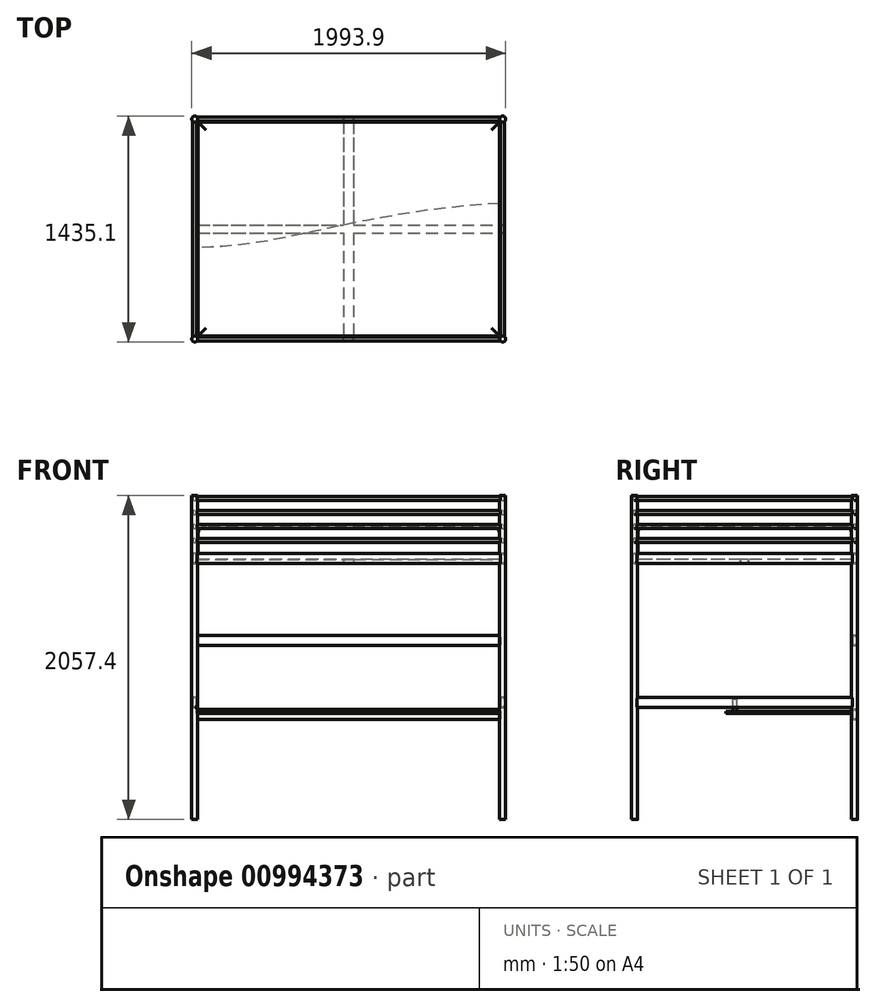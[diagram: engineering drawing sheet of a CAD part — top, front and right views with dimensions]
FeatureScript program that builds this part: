
annotation { "Feature Type Name" : "Feature", "Feature Type Description" : "" }
export const myFeature = defineFeature(function(context is Context, id is Id, definition is map)
    precondition{}
    {
        {
            var Q0;
            Q0=qCreatedBy(makeId("Top.planeOp"),FACE);
            var sketch = newSketch(context, id + "F0", { "sketchPlane" : qUnion([Q0])});
            skLineSegment(sketch, "E0.bottom", {"start": v(977.9, 698.5) * mm, "end": v(-977.9, 698.5) * mm, "construction": true});
            skLineSegment(sketch, "E0.top", {"start": v(977.9, -698.5) * mm, "end": v(-977.9, -698.5) * mm, "construction": true});
            skLineSegment(sketch, "E0.left", {"start": v(977.9, 698.5) * mm, "end": v(977.9, -698.5) * mm, "construction": true});
            skLineSegment(sketch, "E0.right", {"start": v(-977.9, 698.5) * mm, "end": v(-977.9, -698.5) * mm, "construction": true});
            skPoint(sketch, "E0.middle", {"position": v(0, 0) * mm});
            skCircle(sketch, "E1", {"center": v(-977.9, 698.5) * mm, "radius": 19.05 * mm});
            skCircle(sketch, "E2", {"center": v(977.9, 698.5) * mm, "radius": 19.05 * mm});
            skCircle(sketch, "E3", {"center": v(977.9, -698.5) * mm, "radius": 19.05 * mm});
            skCircle(sketch, "E4", {"center": v(-977.9, -698.5) * mm, "radius": 19.05 * mm});
            skSolve(sketch);
        }
        {
            var Q0;
            Q0=makeQuery(id+"F0.imprint","IMPRINT",FACE,{"disambiguationData":[TD([[makeQuery(id+"F0.imprint","IMPRINT",EDGE,{"derivedFrom":sQuery(id+"F0.wireOp",EDGE,"E1")}),1.0]])]});
            var Q1;
            Q1=makeQuery(id+"F0.imprint","IMPRINT",FACE,{"disambiguationData":[TD([[makeQuery(id+"F0.imprint","IMPRINT",EDGE,{"derivedFrom":sQuery(id+"F0.wireOp",EDGE,"E2")}),1.0]])]});
            var Q2;
            Q2=makeQuery(id+"F0.imprint","IMPRINT",FACE,{"disambiguationData":[TD([[makeQuery(id+"F0.imprint","IMPRINT",EDGE,{"derivedFrom":sQuery(id+"F0.wireOp",EDGE,"E3")}),1.0]])]});
            var Q3;
            Q3=makeQuery(id+"F0.imprint","IMPRINT",FACE,{"disambiguationData":[TD([[makeQuery(id+"F0.imprint","IMPRINT",EDGE,{"derivedFrom":sQuery(id+"F0.wireOp",EDGE,"E4")}),1.0]])]});
            extrude(context, id + "F1", {"entities" : qUnion([Q0, Q1, Q2, Q3]), "depth" : 2057.4 * mm, "offsetDistance" : 25.4 * mm});
        }
        {
            var Q0;
            Q0=qCreatedBy(makeId("Right.planeOp"),FACE);
            var sketch = newSketch(context, id + "F2", { "sketchPlane" : qUnion([Q0])});
            skCircle(sketch, "E5", {"center": v(-698.5, 2038.35) * mm, "radius": 12.7 * mm});
            skCircle(sketch, "E6.0.1.0", {"center": v(-698.5, 1949.45) * mm, "radius": 12.7 * mm});
            skCircle(sketch, "E6.0.2.0", {"center": v(-698.5, 1860.55) * mm, "radius": 12.7 * mm});
            skCircle(sketch, "E6.0.3.0", {"center": v(-698.5, 1771.65) * mm, "radius": 12.7 * mm});
            skCircle(sketch, "E6.1.0.0", {"center": v(698.5, 2038.35) * mm, "radius": 12.7 * mm});
            skCircle(sketch, "E6.1.1.0", {"center": v(698.5, 1949.45) * mm, "radius": 12.7 * mm});
            skCircle(sketch, "E6.1.2.0", {"center": v(698.5, 1860.55) * mm, "radius": 12.7 * mm});
            skCircle(sketch, "E6.1.3.0", {"center": v(698.5, 1771.65) * mm, "radius": 12.7 * mm});
            skLineSegment(sketch, "E6.direction1", {"start": v(-698.5, 2038.35) * mm, "end": v(698.5, 2038.35) * mm, "construction": true});
            skLineSegment(sketch, "E6.direction2", {"start": v(-698.5, 2038.35) * mm, "end": v(-698.5, 1949.45) * mm, "construction": true});
            skLineSegment(sketch, "E7.bottom", {"start": v(-697.23, 1689.1) * mm, "end": v(-699.77, 1689.1) * mm});
            skLineSegment(sketch, "E7.top", {"start": v(-697.23, 1625.6) * mm, "end": v(-699.77, 1625.6) * mm});
            skLineSegment(sketch, "E7.left", {"start": v(-685.8, 1677.67) * mm, "end": v(-685.8, 1637.03) * mm});
            skLineSegment(sketch, "E7.right", {"start": v(-711.2, 1677.67) * mm, "end": v(-711.2, 1637.03) * mm});
            skPoint(sketch, "E7.middle", {"position": v(-698.5, 1657.35) * mm});
            skPoint(sketch, "E8.visualSharp", {"position": v(-711.2, 1689.1) * mm});
            skArc(sketch, "E8.filletArc", {"start": v(-699.77, 1689.1) * mm, "mid": v(-707.85, 1685.75) * mm, "end": v(-711.2, 1677.67) * mm});
            skPoint(sketch, "E9.visualSharp", {"position": v(-685.8, 1689.1) * mm});
            skArc(sketch, "E9.filletArc", {"start": v(-685.8, 1677.67) * mm, "mid": v(-689.15, 1685.75) * mm, "end": v(-697.23, 1689.1) * mm});
            skPoint(sketch, "E10.visualSharp", {"position": v(-685.8, 1625.6) * mm});
            skArc(sketch, "E10.filletArc", {"start": v(-697.23, 1625.6) * mm, "mid": v(-689.15, 1628.95) * mm, "end": v(-685.8, 1637.03) * mm});
            skPoint(sketch, "E11.visualSharp", {"position": v(-711.2, 1625.6) * mm});
            skArc(sketch, "E11.filletArc", {"start": v(-711.2, 1637.03) * mm, "mid": v(-707.85, 1628.95) * mm, "end": v(-699.77, 1625.6) * mm});
            skLineSegment(sketch, "E12.MirrorCS", {"start": v(685.8, 1677.67) * mm, "end": v(685.8, 1637.03) * mm});
            skArc(sketch, "E13.MirrorCS", {"start": v(685.8, 1677.67) * mm, "mid": v(689.15, 1685.75) * mm, "end": v(697.23, 1689.1) * mm});
            skLineSegment(sketch, "E14.MirrorCS", {"start": v(697.23, 1689.1) * mm, "end": v(699.77, 1689.1) * mm});
            skArc(sketch, "E15.MirrorCS", {"start": v(699.77, 1689.1) * mm, "mid": v(707.85, 1685.75) * mm, "end": v(711.2, 1677.67) * mm});
            skLineSegment(sketch, "E16.MirrorCS", {"start": v(711.2, 1677.67) * mm, "end": v(711.2, 1637.03) * mm});
            skArc(sketch, "E17.MirrorCS", {"start": v(711.2, 1637.03) * mm, "mid": v(707.85, 1628.95) * mm, "end": v(699.77, 1625.6) * mm});
            skLineSegment(sketch, "E18.MirrorCS", {"start": v(697.23, 1625.6) * mm, "end": v(699.77, 1625.6) * mm});
            skArc(sketch, "E19.MirrorCS", {"start": v(697.23, 1625.6) * mm, "mid": v(689.15, 1628.95) * mm, "end": v(685.8, 1637.03) * mm});
            skLineSegment(sketch, "E20.MirrorCS", {"start": v(685.8, 1156.97) * mm, "end": v(685.8, 1116.33) * mm});
            skArc(sketch, "E21.MirrorCS", {"start": v(685.8, 1156.97) * mm, "mid": v(689.15, 1165.05) * mm, "end": v(697.23, 1168.4) * mm});
            skLineSegment(sketch, "E22.MirrorCS", {"start": v(697.23, 1168.4) * mm, "end": v(699.77, 1168.4) * mm});
            skArc(sketch, "E23.MirrorCS", {"start": v(699.77, 1168.4) * mm, "mid": v(707.85, 1165.05) * mm, "end": v(711.2, 1156.97) * mm});
            skLineSegment(sketch, "E24.MirrorCS", {"start": v(711.2, 1156.97) * mm, "end": v(711.2, 1116.33) * mm});
            skArc(sketch, "E25.MirrorCS", {"start": v(711.2, 1116.33) * mm, "mid": v(707.85, 1108.25) * mm, "end": v(699.77, 1104.9) * mm});
            skLineSegment(sketch, "E26.MirrorCS", {"start": v(697.23, 1104.9) * mm, "end": v(699.77, 1104.9) * mm});
            skArc(sketch, "E27.MirrorCS", {"start": v(697.23, 1104.9) * mm, "mid": v(689.15, 1108.25) * mm, "end": v(685.8, 1116.33) * mm});
            skLineSegment(sketch, "E28.MirrorCS", {"start": v(685.8, 687.19) * mm, "end": v(685.8, 646.55) * mm});
            skArc(sketch, "E29.MirrorCS", {"start": v(685.8, 687.19) * mm, "mid": v(689.15, 695.27) * mm, "end": v(697.23, 698.62) * mm});
            skLineSegment(sketch, "E30.MirrorCS", {"start": v(697.23, 698.62) * mm, "end": v(699.77, 698.62) * mm});
            skArc(sketch, "E31.MirrorCS", {"start": v(699.77, 698.62) * mm, "mid": v(707.85, 695.27) * mm, "end": v(711.2, 687.19) * mm});
            skLineSegment(sketch, "E32.MirrorCS", {"start": v(711.2, 687.19) * mm, "end": v(711.2, 646.55) * mm});
            skArc(sketch, "E33.MirrorCS", {"start": v(711.2, 646.55) * mm, "mid": v(707.85, 638.47) * mm, "end": v(699.77, 635.12) * mm});
            skLineSegment(sketch, "E34.MirrorCS", {"start": v(697.23, 635.12) * mm, "end": v(699.77, 635.12) * mm});
            skArc(sketch, "E35.MirrorCS", {"start": v(697.23, 635.12) * mm, "mid": v(689.15, 638.47) * mm, "end": v(685.8, 646.55) * mm});
            skSolve(sketch);
        }
        {
            var Q0;
            Q0=makeQuery(id+"F2.imprint","IMPRINT",FACE,{"disambiguationData":[TD([[makeQuery(id+"F2.imprint","IMPRINT",EDGE,{"derivedFrom":sQuery(id+"F2.wireOp",EDGE,"E6.0.1.0")}),1.0]])]});
            var Q1;
            Q1=makeQuery(id+"F2.imprint","IMPRINT",FACE,{"disambiguationData":[TD([[makeQuery(id+"F2.imprint","IMPRINT",EDGE,{"derivedFrom":sQuery(id+"F2.wireOp",EDGE,"E5")}),1.0]])]});
            var Q2;
            Q2=makeQuery(id+"F2.imprint","IMPRINT",FACE,{"disambiguationData":[TD([[makeQuery(id+"F2.imprint","IMPRINT",EDGE,{"derivedFrom":sQuery(id+"F2.wireOp",EDGE,"E6.0.2.0")}),1.0]])]});
            var Q3;
            Q3=makeQuery(id+"F2.imprint","IMPRINT",FACE,{"disambiguationData":[TD([[makeQuery(id+"F2.imprint","IMPRINT",EDGE,{"derivedFrom":sQuery(id+"F2.wireOp",EDGE,"E6.0.3.0")}),1.0]])]});
            var Q4;
            Q4=makeQuery(id+"F2.imprint","IMPRINT",FACE,{"disambiguationData":[TD([[makeQuery(id+"F2.imprint","IMPRINT",EDGE,{"derivedFrom":sQuery(id+"F2.wireOp",EDGE,"E6.1.3.0")}),1.0]])]});
            var Q5;
            Q5=makeQuery(id+"F2.imprint","IMPRINT",FACE,{"disambiguationData":[TD([[makeQuery(id+"F2.imprint","IMPRINT",EDGE,{"derivedFrom":sQuery(id+"F2.wireOp",EDGE,"E6.1.2.0")}),1.0]])]});
            var Q6;
            Q6=makeQuery(id+"F2.imprint","IMPRINT",FACE,{"disambiguationData":[TD([[makeQuery(id+"F2.imprint","IMPRINT",EDGE,{"derivedFrom":sQuery(id+"F2.wireOp",EDGE,"E6.1.1.0")}),1.0]])]});
            var Q7;
            Q7=makeQuery(id+"F2.imprint","IMPRINT",FACE,{"disambiguationData":[TD([[makeQuery(id+"F2.imprint","IMPRINT",EDGE,{"derivedFrom":sQuery(id+"F2.wireOp",EDGE,"E6.1.0.0")}),1.0]])]});
            var Q8;
            Q8=makeQuery(id+"F2.imprint","IMPRINT",FACE,{"disambiguationData":[TD([[makeQuery(id+"F2.imprint","IMPRINT",EDGE,{"derivedFrom":sQuery(id+"F2.wireOp",EDGE,"E7.bottom")}),1.0]])]});
            var Q9;
            Q9=makeQuery(id+"F2.imprint","IMPRINT",FACE,{"disambiguationData":[TD([[makeQuery(id+"F2.imprint","IMPRINT",EDGE,{"derivedFrom":sQuery(id+"F2.wireOp",EDGE,"E12.MirrorCS")}),1.0]])]});
            var Q10;
            Q10=makeQuery(id+"F2.imprint","IMPRINT",FACE,{"disambiguationData":[TD([[makeQuery(id+"F2.imprint","IMPRINT",EDGE,{"derivedFrom":sQuery(id+"F2.wireOp",EDGE,"E20.MirrorCS")}),1.0]])]});
            var Q11;
            Q11=makeQuery(id+"F2.imprint","IMPRINT",FACE,{"disambiguationData":[TD([[makeQuery(id+"F2.imprint","IMPRINT",EDGE,{"derivedFrom":sQuery(id+"F2.wireOp",EDGE,"E28.MirrorCS")}),1.0]])]});
            var Q12;
            Q12=sQuery(id+"F2.wireOp",EDGE,"E5");
            var Q13;
            Q13=sQuery(id+"F2.wireOp",EDGE,"E6.0.1.0");
            var Q14;
            Q14=sQuery(id+"F2.wireOp",EDGE,"E6.0.2.0");
            var Q15;
            Q15=sQuery(id+"F2.wireOp",EDGE,"E6.0.3.0");
            var Q16;
            Q16=sQuery(id+"F2.wireOp",EDGE,"E6.1.3.0");
            var Q17;
            Q17=sQuery(id+"F2.wireOp",EDGE,"E6.1.2.0");
            var Q18;
            Q18=sQuery(id+"F2.wireOp",EDGE,"E6.1.1.0");
            var Q19;
            Q19=sQuery(id+"F2.wireOp",EDGE,"E6.1.0.0");
            extrude(context, id + "F3", {"entities" : qUnion([Q0, Q1, Q2, Q3, Q4, Q5, Q6, Q7, Q8, Q9, Q10, Q11]), "operationType" : NewBodyOperationType.ADD, "surfaceEntities" : qUnion([Q12, Q13, Q14, Q15, Q16, Q17, Q18, Q19]), "depth" : 1974.6 * mm, "offsetDistance" : 25.4 * mm, "symmetric" : true});
        }
        {
            var Q0;
            Q0=qCreatedBy(makeId("Front.planeOp"),FACE);
            var sketch = newSketch(context, id + "F4", { "sketchPlane" : qUnion([Q0])});
            skCircle(sketch, "E36", {"center": v(-977.9, 2038.35) * mm, "radius": 12.7 * mm});
            skCircle(sketch, "E37.0.1.0", {"center": v(-977.9, 1949.45) * mm, "radius": 12.7 * mm});
            skCircle(sketch, "E37.0.2.0", {"center": v(-977.9, 1860.55) * mm, "radius": 12.7 * mm});
            skCircle(sketch, "E37.0.3.0", {"center": v(-977.9, 1771.65) * mm, "radius": 12.7 * mm});
            skCircle(sketch, "E37.1.0.0", {"center": v(977.9, 2038.35) * mm, "radius": 12.7 * mm});
            skCircle(sketch, "E37.1.1.0", {"center": v(977.9, 1949.45) * mm, "radius": 12.7 * mm});
            skCircle(sketch, "E37.1.2.0", {"center": v(977.9, 1860.55) * mm, "radius": 12.7 * mm});
            skCircle(sketch, "E37.1.3.0", {"center": v(977.9, 1771.65) * mm, "radius": 12.7 * mm});
            skLineSegment(sketch, "E37.direction1", {"start": v(-977.9, 2038.35) * mm, "end": v(977.9, 2038.35) * mm, "construction": true});
            skLineSegment(sketch, "E37.direction2", {"start": v(-977.9, 2038.35) * mm, "end": v(-977.9, 1949.45) * mm, "construction": true});
            skLineSegment(sketch, "E38.bottom", {"start": v(-976.63, 1689.1) * mm, "end": v(-979.17, 1689.1) * mm});
            skLineSegment(sketch, "E38.top", {"start": v(-976.63, 1625.6) * mm, "end": v(-979.17, 1625.6) * mm});
            skLineSegment(sketch, "E38.left", {"start": v(-965.2, 1677.67) * mm, "end": v(-965.2, 1637.03) * mm});
            skLineSegment(sketch, "E38.right", {"start": v(-990.6, 1677.67) * mm, "end": v(-990.6, 1637.03) * mm});
            skPoint(sketch, "E38.middle", {"position": v(-977.9, 1657.35) * mm});
            skPoint(sketch, "E39.visualSharp", {"position": v(-990.6, 1689.1) * mm});
            skArc(sketch, "E39.filletArc", {"start": v(-979.17, 1689.1) * mm, "mid": v(-987.25, 1685.75) * mm, "end": v(-990.6, 1677.67) * mm});
            skPoint(sketch, "E40.visualSharp", {"position": v(-965.2, 1689.1) * mm});
            skArc(sketch, "E40.filletArc", {"start": v(-965.2, 1677.67) * mm, "mid": v(-968.55, 1685.75) * mm, "end": v(-976.63, 1689.1) * mm});
            skPoint(sketch, "E41.visualSharp", {"position": v(-965.2, 1625.6) * mm});
            skArc(sketch, "E41.filletArc", {"start": v(-976.63, 1625.6) * mm, "mid": v(-968.55, 1628.95) * mm, "end": v(-965.2, 1637.03) * mm});
            skPoint(sketch, "E42.visualSharp", {"position": v(-990.6, 1625.6) * mm});
            skArc(sketch, "E42.filletArc", {"start": v(-990.6, 1637.03) * mm, "mid": v(-987.25, 1628.95) * mm, "end": v(-979.17, 1625.6) * mm});
            skLineSegment(sketch, "E43.MirrorCS", {"start": v(965.2, 1677.67) * mm, "end": v(965.2, 1637.03) * mm});
            skArc(sketch, "E44.MirrorCS", {"start": v(965.2, 1677.67) * mm, "mid": v(968.55, 1685.75) * mm, "end": v(976.63, 1689.1) * mm});
            skLineSegment(sketch, "E45.MirrorCS", {"start": v(976.63, 1689.1) * mm, "end": v(979.17, 1689.1) * mm});
            skArc(sketch, "E46.MirrorCS", {"start": v(979.17, 1689.1) * mm, "mid": v(987.25, 1685.75) * mm, "end": v(990.6, 1677.67) * mm});
            skLineSegment(sketch, "E47.MirrorCS", {"start": v(990.6, 1677.67) * mm, "end": v(990.6, 1637.03) * mm});
            skArc(sketch, "E48.MirrorCS", {"start": v(990.6, 1637.03) * mm, "mid": v(987.25, 1628.95) * mm, "end": v(979.17, 1625.6) * mm});
            skLineSegment(sketch, "E49.MirrorCS", {"start": v(976.63, 1625.6) * mm, "end": v(979.17, 1625.6) * mm});
            skArc(sketch, "E50.MirrorCS", {"start": v(976.63, 1625.6) * mm, "mid": v(968.55, 1628.95) * mm, "end": v(965.2, 1637.03) * mm});
            skPoint(sketch, "E51.0.1.0", {"position": v(-990.6, 711.2) * mm});
            skArc(sketch, "E51.0.1.1", {"start": v(-965.2, 763.27) * mm, "mid": v(-968.55, 771.35) * mm, "end": v(-976.63, 774.7) * mm});
            skArc(sketch, "E51.0.1.2", {"start": v(-979.17, 774.7) * mm, "mid": v(-987.25, 771.35) * mm, "end": v(-990.6, 763.27) * mm});
            skLineSegment(sketch, "E51.0.1.3", {"start": v(-965.2, 763.27) * mm, "end": v(-965.2, 722.63) * mm});
            skPoint(sketch, "E51.0.1.4", {"position": v(-965.2, 774.7) * mm});
            skPoint(sketch, "E51.0.1.5", {"position": v(-977.9, 742.95) * mm});
            skPoint(sketch, "E51.0.1.6", {"position": v(-990.6, 774.7) * mm});
            skPoint(sketch, "E51.0.1.7", {"position": v(-965.2, 711.2) * mm});
            skLineSegment(sketch, "E51.0.1.8", {"start": v(-990.6, 763.27) * mm, "end": v(-990.6, 722.63) * mm});
            skArc(sketch, "E51.0.1.9", {"start": v(-990.6, 722.63) * mm, "mid": v(-987.25, 714.55) * mm, "end": v(-979.17, 711.2) * mm});
            skArc(sketch, "E51.0.1.10", {"start": v(-976.63, 711.2) * mm, "mid": v(-968.55, 714.55) * mm, "end": v(-965.2, 722.63) * mm});
            skLineSegment(sketch, "E51.0.1.11", {"start": v(-976.63, 774.7) * mm, "end": v(-979.17, 774.7) * mm});
            skLineSegment(sketch, "E51.0.1.12", {"start": v(-976.63, 711.2) * mm, "end": v(-979.17, 711.2) * mm});
            skPoint(sketch, "E51.1.0.0", {"position": v(965.2, 1625.6) * mm});
            skArc(sketch, "E51.1.0.1", {"start": v(990.6, 1677.67) * mm, "mid": v(987.25, 1685.75) * mm, "end": v(979.17, 1689.1) * mm});
            skArc(sketch, "E51.1.0.2", {"start": v(976.63, 1689.1) * mm, "mid": v(968.55, 1685.75) * mm, "end": v(965.2, 1677.67) * mm});
            skPoint(sketch, "E51.1.0.4", {"position": v(990.6, 1689.1) * mm});
            skPoint(sketch, "E51.1.0.5", {"position": v(977.9, 1657.35) * mm});
            skPoint(sketch, "E51.1.0.6", {"position": v(965.2, 1689.1) * mm});
            skPoint(sketch, "E51.1.0.7", {"position": v(990.6, 1625.6) * mm});
            skArc(sketch, "E51.1.0.9", {"start": v(965.2, 1637.03) * mm, "mid": v(968.55, 1628.95) * mm, "end": v(976.63, 1625.6) * mm});
            skArc(sketch, "E51.1.0.10", {"start": v(979.17, 1625.6) * mm, "mid": v(987.25, 1628.95) * mm, "end": v(990.6, 1637.03) * mm});
            skLineSegment(sketch, "E51.1.0.11", {"start": v(979.17, 1689.1) * mm, "end": v(976.63, 1689.1) * mm});
            skLineSegment(sketch, "E51.1.0.12", {"start": v(979.17, 1625.6) * mm, "end": v(976.63, 1625.6) * mm});
            skPoint(sketch, "E51.1.1.0", {"position": v(965.2, 711.2) * mm});
            skArc(sketch, "E51.1.1.1", {"start": v(990.6, 763.27) * mm, "mid": v(987.25, 771.35) * mm, "end": v(979.17, 774.7) * mm});
            skArc(sketch, "E51.1.1.2", {"start": v(976.63, 774.7) * mm, "mid": v(968.55, 771.35) * mm, "end": v(965.2, 763.27) * mm});
            skLineSegment(sketch, "E51.1.1.3", {"start": v(990.6, 763.27) * mm, "end": v(990.6, 722.63) * mm});
            skPoint(sketch, "E51.1.1.4", {"position": v(990.6, 774.7) * mm});
            skPoint(sketch, "E51.1.1.5", {"position": v(977.9, 742.95) * mm});
            skPoint(sketch, "E51.1.1.6", {"position": v(965.2, 774.7) * mm});
            skPoint(sketch, "E51.1.1.7", {"position": v(990.6, 711.2) * mm});
            skLineSegment(sketch, "E51.1.1.8", {"start": v(965.2, 763.27) * mm, "end": v(965.2, 722.63) * mm});
            skArc(sketch, "E51.1.1.9", {"start": v(965.2, 722.63) * mm, "mid": v(968.55, 714.55) * mm, "end": v(976.63, 711.2) * mm});
            skArc(sketch, "E51.1.1.10", {"start": v(979.17, 711.2) * mm, "mid": v(987.25, 714.55) * mm, "end": v(990.6, 722.63) * mm});
            skLineSegment(sketch, "E51.1.1.11", {"start": v(979.17, 774.7) * mm, "end": v(976.63, 774.7) * mm});
            skLineSegment(sketch, "E51.1.1.12", {"start": v(979.17, 711.2) * mm, "end": v(976.63, 711.2) * mm});
            skLineSegment(sketch, "E51.direction1", {"start": v(-990.6, 1625.6) * mm, "end": v(965.2, 1625.6) * mm, "construction": true});
            skLineSegment(sketch, "E51.direction2", {"start": v(-990.6, 1625.6) * mm, "end": v(-990.6, 711.2) * mm, "construction": true});
            skSolve(sketch);
        }
        {
            var Q0;
            Q0=makeQuery(id+"F4.imprint","IMPRINT",FACE,{"disambiguationData":[TD([[makeQuery(id+"F4.imprint","IMPRINT",EDGE,{"derivedFrom":sQuery(id+"F4.wireOp",EDGE,"E37.1.0.0")}),1.0]])]});
            var Q1;
            Q1=makeQuery(id+"F4.imprint","IMPRINT",FACE,{"disambiguationData":[TD([[makeQuery(id+"F4.imprint","IMPRINT",EDGE,{"derivedFrom":sQuery(id+"F4.wireOp",EDGE,"E37.1.1.0")}),1.0]])]});
            var Q2;
            Q2=makeQuery(id+"F4.imprint","IMPRINT",FACE,{"disambiguationData":[TD([[makeQuery(id+"F4.imprint","IMPRINT",EDGE,{"derivedFrom":sQuery(id+"F4.wireOp",EDGE,"E37.1.2.0")}),1.0]])]});
            var Q3;
            Q3=makeQuery(id+"F4.imprint","IMPRINT",FACE,{"disambiguationData":[TD([[makeQuery(id+"F4.imprint","IMPRINT",EDGE,{"derivedFrom":sQuery(id+"F4.wireOp",EDGE,"E37.1.3.0")}),1.0]])]});
            var Q4;
            Q4=makeQuery(id+"F4.imprint","IMPRINT",FACE,{"disambiguationData":[TD([[makeQuery(id+"F4.imprint","IMPRINT",EDGE,{"derivedFrom":sQuery(id+"F4.wireOp",EDGE,"E37.0.3.0")}),1.0]])]});
            var Q5;
            Q5=makeQuery(id+"F4.imprint","IMPRINT",FACE,{"disambiguationData":[TD([[makeQuery(id+"F4.imprint","IMPRINT",EDGE,{"derivedFrom":sQuery(id+"F4.wireOp",EDGE,"E37.0.2.0")}),1.0]])]});
            var Q6;
            Q6=makeQuery(id+"F4.imprint","IMPRINT",FACE,{"disambiguationData":[TD([[makeQuery(id+"F4.imprint","IMPRINT",EDGE,{"derivedFrom":sQuery(id+"F4.wireOp",EDGE,"E37.0.1.0")}),1.0]])]});
            var Q7;
            Q7=makeQuery(id+"F4.imprint","IMPRINT",FACE,{"disambiguationData":[TD([[makeQuery(id+"F4.imprint","IMPRINT",EDGE,{"derivedFrom":sQuery(id+"F4.wireOp",EDGE,"E36")}),1.0]])]});
            var Q8;
            Q8=makeQuery(id+"F4.imprint","IMPRINT",FACE,{"disambiguationData":[TD([[makeQuery(id+"F4.imprint","IMPRINT",EDGE,{"derivedFrom":sQuery(id+"F4.wireOp",EDGE,"E38.bottom")}),1.0]])]});
            var Q9;
            Q9=makeQuery(id+"F4.imprint","IMPRINT",FACE,{"disambiguationData":[TD([[makeQuery(id+"F4.imprint","IMPRINT",EDGE,{"derivedFrom":sQuery(id+"F4.wireOp",EDGE,"E43.MirrorCS")}),1.0]])]});
            var Q10;
            Q10=makeQuery(id+"F4.imprint","IMPRINT",FACE,{"disambiguationData":[TD([[makeQuery(id+"F4.imprint","IMPRINT",EDGE,{"derivedFrom":sQuery(id+"F4.wireOp",EDGE,"E51.0.1.1")}),1.0]])]});
            var Q11;
            Q11=makeQuery(id+"F4.imprint","IMPRINT",FACE,{"disambiguationData":[TD([[makeQuery(id+"F4.imprint","IMPRINT",EDGE,{"derivedFrom":sQuery(id+"F4.wireOp",EDGE,"E51.1.1.1")}),1.0]])]});
            var Q12;
            Q12=makeQuery(id+"F4.imprint","IMPRINT",FACE,{"disambiguationData":[TD([[makeQuery(id+"F4.imprint","IMPRINT",EDGE,{"derivedFrom":sQuery(id+"F4.wireOp",EDGE,"E51.1.0.1")}),1.0]])]});
            extrude(context, id + "F5", {"entities" : qUnion([Q0, Q1, Q2, Q3, Q4, Q5, Q6, Q7, Q8, Q9, Q10, Q11, Q12]), "operationType" : NewBodyOperationType.ADD, "depth" : 1406.65 * mm, "offsetDistance" : 25.4 * mm, "symmetric" : true});
        }
        {
            var Q0;
            Q0=qCreatedBy(makeId("Top.planeOp"),FACE);
            var sketch = newSketch(context, id + "F6", { "sketchPlane" : qUnion([Q0])});
            skLineSegment(sketch, "E52.bottom", {"start": v(31.75, 698.5) * mm, "end": v(-31.75, 698.5) * mm});
            skLineSegment(sketch, "E52.top", {"start": v(31.75, -698.5) * mm, "end": v(-31.75, -698.5) * mm});
            skLineSegment(sketch, "E52.left", {"start": v(31.75, 698.5) * mm, "end": v(31.75, -698.5) * mm});
            skLineSegment(sketch, "E52.right", {"start": v(-31.75, 698.5) * mm, "end": v(-31.75, -698.5) * mm});
            skPoint(sketch, "E52.middle", {"position": v(0, 0) * mm});
            skLineSegment(sketch, "E53.bottom", {"start": v(-977.9, 25.4) * mm, "end": v(977.9, 25.4) * mm});
            skLineSegment(sketch, "E53.top", {"start": v(-977.9, -25.4) * mm, "end": v(977.9, -25.4) * mm});
            skLineSegment(sketch, "E53.left", {"start": v(-977.9, 25.4) * mm, "end": v(-977.9, -25.4) * mm});
            skLineSegment(sketch, "E53.right", {"start": v(977.9, 25.4) * mm, "end": v(977.9, -25.4) * mm});
            skSolve(sketch);
        }
        {
            var Q0;
            {var subQ0=sQuery(id+"F6.wireOp",EDGE,"E52.bottom");Q0=makeQuery(id+"F6.imprint","IMPRINT",FACE,{"disambiguationData":[TD([[makeQuery(id+"F6.imprint","IMPRINT",EDGE,{"derivedFrom":subQ0}),1.0]])]});}
            var Q1;
            {var subQ5=sQuery(id+"F6.wireOp",EDGE,"E53.left");Q1=makeQuery(id+"F6.imprint","IMPRINT",FACE,{"disambiguationData":[TD([[makeQuery(id+"F6.imprint","IMPRINT",EDGE,{"derivedFrom":subQ5}),1.0]])]});}
            var Q2;
            {var subQ5=sQuery(id+"F6.wireOp",EDGE,"E53.right");Q2=makeQuery(id+"F6.imprint","IMPRINT",FACE,{"disambiguationData":[TD([[makeQuery(id+"F6.imprint","IMPRINT",EDGE,{"derivedFrom":subQ5}),-1.0]])]});}
            var Q3;
            {var subQ0=sQuery(id+"F6.wireOp",EDGE,"E52.top");Q3=makeQuery(id+"F6.imprint","IMPRINT",FACE,{"disambiguationData":[TD([[makeQuery(id+"F6.imprint","IMPRINT",EDGE,{"derivedFrom":subQ0}),-1.0]])]});}
            var Q4;
            {var subQ0=sQuery(id+"F6.wireOp",EDGE,"E53.bottom");var subQ1=sQuery(id+"F6.wireOp",EDGE,"E52.left");var subQ2=makeQuery(id+"F6.imprint","INTERSECT",VERTEX,{"derivedFrom":[subQ1,subQ0]});Q4=makeQuery(id+"F6.imprint","IMPRINT",FACE,{"disambiguationData":[TD([[makeQuery(id+"F6.imprint","IMPRINT",EDGE,{"disambiguationData":[TD([[subQ2,-1.0]])],"derivedFrom":subQ1}),-1.0]])]});}
            extrude(context, id + "F7", {"entities" : qUnion([Q0, Q1, Q2, Q3, Q4]), "operationType" : NewBodyOperationType.ADD, "depth" : 1651 * mm, "offsetDistance" : 25.4 * mm, "hasSecondDirection" : true, "secondDirectionOppositeDirection" : false, "secondDirectionDepth" : 1625.6 * mm});
        }
        {
            var Q0;
            Q0=makeQuery(id+"F7.opExtrude","CAP_FACE",FACE,{"disambiguationData":[OSD([sQuery(id+"F6.wireOp",EDGE,"E52.bottom"),sQuery(id+"F6.wireOp",EDGE,"E52.top"),sQuery(id+"F6.wireOp",EDGE,"E52.left"),sQuery(id+"F6.wireOp",EDGE,"E52.right"),sQuery(id+"F6.wireOp",EDGE,"E53.bottom"),sQuery(id+"F6.wireOp",EDGE,"E53.top"),sQuery(id+"F6.wireOp",EDGE,"E53.left"),sQuery(id+"F6.wireOp",EDGE,"E53.right")])],"isStart":false});
            var sketch = newSketch(context, id + "F8", { "sketchPlane" : qUnion([Q0])});
            skLineSegment(sketch, "E54.bottom", {"start": v(957.01, 679.11) * mm, "end": v(-957.01, 679.11) * mm});
            skLineSegment(sketch, "E54.top", {"start": v(957.01, -679.11) * mm, "end": v(-957.01, -679.11) * mm});
            skLineSegment(sketch, "E54.left", {"start": v(957.01, 679.11) * mm, "end": v(957.01, -679.11) * mm});
            skLineSegment(sketch, "E54.right", {"start": v(-957.01, 679.11) * mm, "end": v(-957.01, -679.11) * mm});
            skPoint(sketch, "E54.middle", {"position": v(0, 0) * mm});
            skSolve(sketch);
        }
        {
            var Q0;
            {var subQ0=sQuery(id+"F8.wireOp",EDGE,"E54.right");var subQ1=sQuery(id+"F8.wireOp",EDGE,"E54.bottom");var subQ2=makeQuery(id+"F8.imprint","INTERSECT",VERTEX,{"derivedFrom":[subQ1,subQ0]});Q0=makeQuery(id+"F8.imprint","IMPRINT",FACE,{"disambiguationData":[TD([[makeQuery(id+"F8.imprint","IMPRINT",EDGE,{"disambiguationData":[TD([[subQ2,1.0]])],"derivedFrom":subQ1}),1.0]])]});}
            var Q1;
            {var subQ0=sQuery(id+"F8.wireOp",EDGE,"E54.left");var subQ1=sQuery(id+"F8.wireOp",EDGE,"E54.bottom");var subQ2=makeQuery(id+"F8.imprint","INTERSECT",VERTEX,{"derivedFrom":[subQ1,subQ0]});Q1=makeQuery(id+"F8.imprint","IMPRINT",FACE,{"disambiguationData":[TD([[makeQuery(id+"F8.imprint","IMPRINT",EDGE,{"disambiguationData":[TD([[subQ2,-1.0]])],"derivedFrom":subQ1}),1.0]])]});}
            var Q2;
            {var subQ0=sQuery(id+"F8.wireOp",EDGE,"E54.left");var subQ1=sQuery(id+"F8.wireOp",EDGE,"E54.top");var subQ2=makeQuery(id+"F8.imprint","INTERSECT",VERTEX,{"derivedFrom":[subQ1,subQ0]});Q2=makeQuery(id+"F8.imprint","IMPRINT",FACE,{"disambiguationData":[TD([[makeQuery(id+"F8.imprint","IMPRINT",EDGE,{"disambiguationData":[TD([[subQ2,-1.0]])],"derivedFrom":subQ1}),-1.0]])]});}
            var Q3;
            {var subQ0=sQuery(id+"F8.wireOp",EDGE,"E54.right");var subQ1=sQuery(id+"F8.wireOp",EDGE,"E54.top");var subQ2=makeQuery(id+"F8.imprint","INTERSECT",VERTEX,{"derivedFrom":[subQ1,subQ0]});Q3=makeQuery(id+"F8.imprint","IMPRINT",FACE,{"disambiguationData":[TD([[makeQuery(id+"F8.imprint","IMPRINT",EDGE,{"disambiguationData":[TD([[subQ2,1.0]])],"derivedFrom":subQ1}),-1.0]])]});}
            var Q4;
            {var subQ2=sQuery(id+"F6.wireOp",EDGE,"E52.left");var subQ5=sQuery(id+"F6.wireOp",EDGE,"E52.bottom");var subQ6=makeQuery(id+"F7.opExtrude","CAP_EDGE",EDGE,{"disambiguationData":[OSD([subQ2]),TDD([makeQuery(id+"F6.imprint","IMPRINT",EDGE,{"disambiguationData":[TD([[makeQuery(id+"F6.imprint","INTERSECT",VERTEX,{"derivedFrom":[subQ5,subQ2]}),-1.0]])],"derivedFrom":subQ2})])],"isStart":false});var subQ29=sQuery(id+"F8.wireOp",EDGE,"E54.bottom");var subQ30=makeQuery(id+"F8.imprint","INTERSECT",VERTEX,{"derivedFrom":[subQ6,subQ29]});Q4=makeQuery(id+"F8.imprint","IMPRINT",FACE,{"disambiguationData":[TD([[makeQuery(id+"F8.imprint","IMPRINT",EDGE,{"disambiguationData":[TD([[subQ30,-1.0]])],"derivedFrom":subQ29}),1.0]])]});}
            extrude(context, id + "F9", {"entities" : qUnion([Q0, Q1, Q2, Q3, Q4]), "depth" : 213.36 * mm, "offsetDistance" : 25.4 * mm});
        }
        {
            var Q0;
            Q0=makeQuery(id+"F9.opExtrude","CAP_EDGE",EDGE,{"disambiguationData":[OSD([sQuery(id+"F8.wireOp",EDGE,"E54.bottom")])],"isStart":false});
            var Q1;
            Q1=makeQuery(id+"F9.opExtrude","CAP_EDGE",EDGE,{"disambiguationData":[OSD([sQuery(id+"F8.wireOp",EDGE,"E54.left")])],"isStart":false});
            var Q2;
            Q2=makeQuery(id+"F9.opExtrude","CAP_EDGE",EDGE,{"disambiguationData":[OSD([sQuery(id+"F8.wireOp",EDGE,"E54.top")])],"isStart":false});
            var Q3;
            Q3=makeQuery(id+"F9.opExtrude","CAP_EDGE",EDGE,{"disambiguationData":[OSD([sQuery(id+"F8.wireOp",EDGE,"E54.right")])],"isStart":false});
            fillet(context, id + "F10", {"entities" : qUnion([Q0, Q1, Q2, Q3]), "radius" : 50.8 * mm, "tangentPropagation" : true, "allowEdgeOverflow" : false});
        }
        {
            var Q0;
            Q0=qCreatedBy(makeId("Top.planeOp"),FACE);
            var sketch = newSketch(context, id + "F11", { "sketchPlane" : qUnion([Q0])});
            skLineSegment(sketch, "E55", {"start": v(-958.85, 695.26) * mm, "end": v(958.85, 695.26) * mm});
            skLineSegment(sketch, "E56", {"start": v(958.85, 695.26) * mm, "end": v(958.85, 161.86) * mm});
            skLineSegment(sketch, "E57", {"start": v(-958.85, 695.26) * mm, "end": v(-958.85, -117.54) * mm});
            skFitSpline(sketch, "E58", {"points": [v(958.85, 161.86) * mm, v(-47.5, 22.16) * mm, v(-548.11, -80.8) * mm, v(-958.85, -117.54) * mm], "startDerivative": vector(-2611.82, -114.4) * mm, "endDerivative": vector(-2065.77, -78.28) * mm});
            skSolve(sketch);
        }
        {
            var Q0;
            Q0=makeQuery(id+"F11.imprint","IMPRINT",FACE,{"disambiguationData":[TD([[makeQuery(id+"F11.imprint","IMPRINT",EDGE,{"derivedFrom":sQuery(id+"F11.wireOp",EDGE,"E55")}),-1.0]])]});
            extrude(context, id + "F12", {"entities" : qUnion([Q0]), "operationType" : NewBodyOperationType.ADD, "depth" : 685.8 * mm, "offsetDistance" : 25.4 * mm, "hasSecondDirection" : true, "secondDirectionOppositeDirection" : false, "secondDirectionDepth" : 673.1 * mm});
        }
        {
            var Q0;
            Q0=makeQuery(id+"F12.opExtrude","SWEPT_FACE",FACE,{"disambiguationData":[OSD([sQuery(id+"F11.wireOp",EDGE,"E57")])]});
            var sketch = newSketch(context, id + "F13", { "sketchPlane" : qUnion([Q0])});
            skLineSegment(sketch, "E59.bottom", {"start": v(73.1, 673.1) * mm, "end": v(47.7, 673.1) * mm});
            skLineSegment(sketch, "E59.top", {"start": v(73.1, 765.45) * mm, "end": v(47.7, 765.45) * mm});
            skLineSegment(sketch, "E59.left", {"start": v(73.1, 673.1) * mm, "end": v(73.1, 765.45) * mm});
            skLineSegment(sketch, "E59.right", {"start": v(47.7, 673.1) * mm, "end": v(47.7, 765.45) * mm});
            skSolve(sketch);
        }
        {
            var Q0;
            {var subQ0=sQuery(id+"F13.wireOp",EDGE,"E59.top");Q0=makeQuery(id+"F13.imprint","IMPRINT",FACE,{"disambiguationData":[TD([[makeQuery(id+"F13.imprint","IMPRINT",EDGE,{"derivedFrom":subQ0}),1.0]])]});}
            var Q1;
            {var subQ0=sQuery(id+"F13.wireOp",EDGE,"E59.bottom");Q1=makeQuery(id+"F13.imprint","IMPRINT",FACE,{"disambiguationData":[TD([[makeQuery(id+"F13.imprint","IMPRINT",EDGE,{"derivedFrom":subQ0}),1.0]])]});}
            extrude(context, id + "F14", {"entities" : qUnion([Q0, Q1]), "operationType" : NewBodyOperationType.ADD, "depth" : 7.62 * mm, "offsetDistance" : 25.4 * mm});
        }
    });
